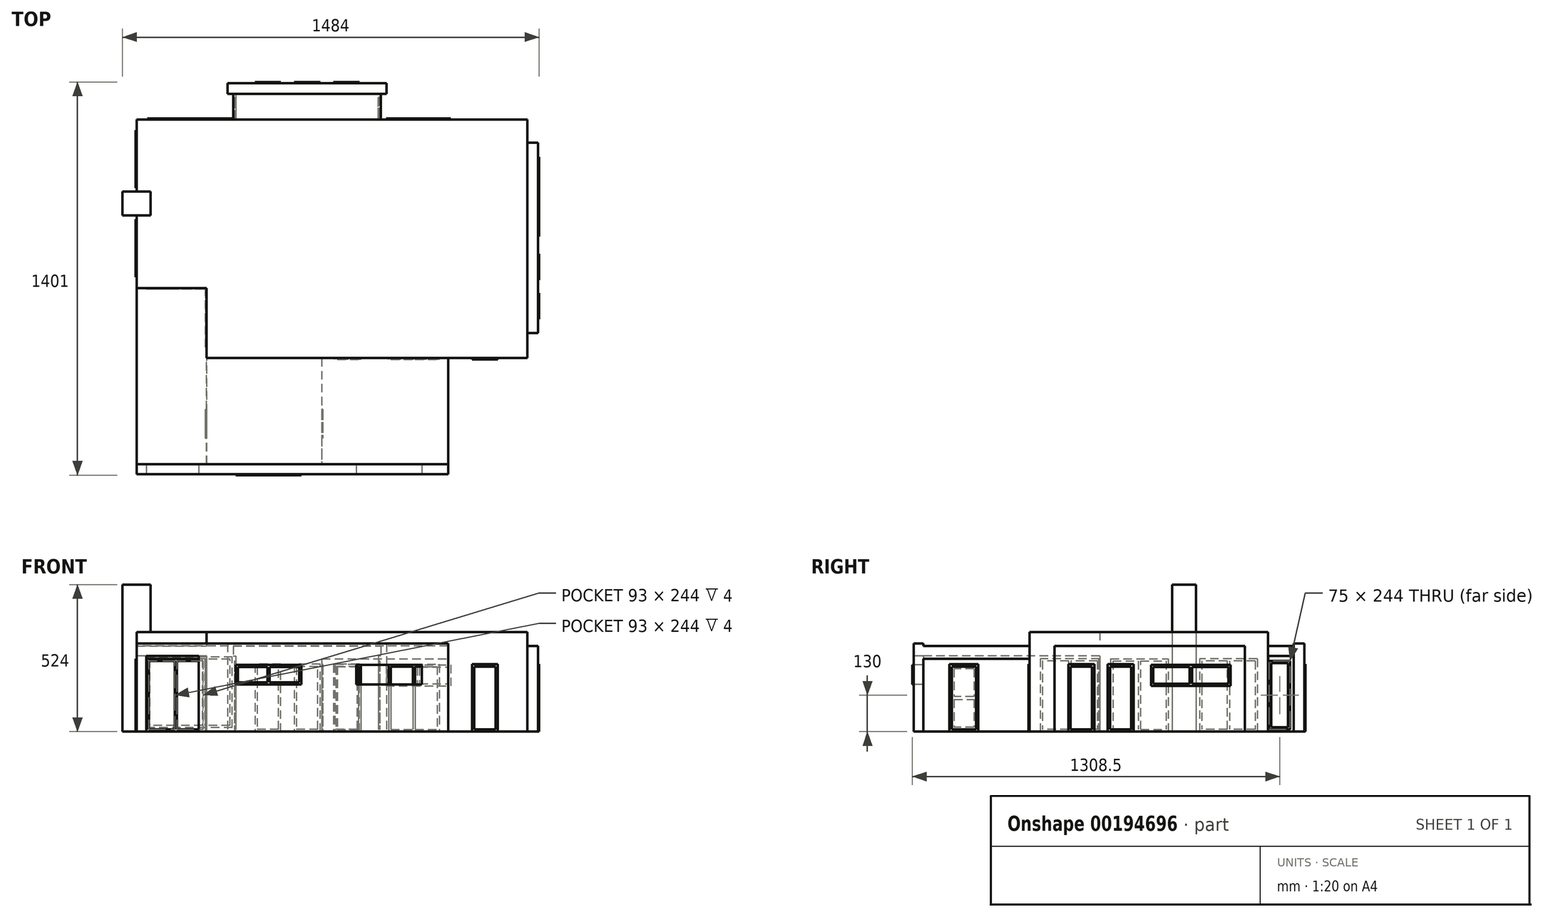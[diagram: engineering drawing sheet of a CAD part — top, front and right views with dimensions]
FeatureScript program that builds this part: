
annotation { "Feature Type Name" : "Feature", "Feature Type Description" : "" }
export const myFeature = defineFeature(function(context is Context, id is Id, definition is map)
    precondition{}
    {
        {
            var Q0;
            Q0=qCreatedBy(makeId("Top.planeOp"),FACE);
            var sketch = newSketch(context, id + "F0", { "sketchPlane" : qUnion([Q0])});
            skLineSegment(sketch, "E0", {"start": v(-692.82, 559.06) * mm, "end": v(699.18, 559.06) * mm});
            skLineSegment(sketch, "E1", {"start": v(699.18, 559.06) * mm, "end": v(699.18, -290.94) * mm});
            skLineSegment(sketch, "E2", {"start": v(699.18, -290.94) * mm, "end": v(-692.82, -290.94) * mm});
            skLineSegment(sketch, "E3", {"start": v(-692.82, -290.94) * mm, "end": v(-692.82, 559.06) * mm});
            skLineSegment(sketch, "E4", {"start": v(-692.82, -40.94) * mm, "end": v(-442.82, -40.94) * mm});
            skLineSegment(sketch, "E5", {"start": v(-442.82, -40.94) * mm, "end": v(-442.82, -290.94) * mm});
            skLineSegment(sketch, "E6", {"start": v(417.18, -290.94) * mm, "end": v(417.18, -668.94) * mm});
            skLineSegment(sketch, "E7", {"start": v(417.18, -668.94) * mm, "end": v(-692.82, -668.94) * mm});
            skLineSegment(sketch, "E8", {"start": v(-692.82, -668.94) * mm, "end": v(-692.82, -290.94) * mm});
            skLineSegment(sketch, "E9", {"start": v(-692.82, 302.06) * mm, "end": v(-642.82, 302.06) * mm});
            skLineSegment(sketch, "E10", {"start": v(-642.82, 302.06) * mm, "end": v(-642.82, 217.06) * mm});
            skLineSegment(sketch, "E11", {"start": v(-642.82, 217.06) * mm, "end": v(-692.82, 217.06) * mm});
            skLineSegment(sketch, "E12.MirrorCS", {"start": v(-692.82, 302.06) * mm, "end": v(-742.82, 302.06) * mm});
            skLineSegment(sketch, "E13.MirrorCS", {"start": v(-742.82, 302.06) * mm, "end": v(-742.82, 217.06) * mm});
            skLineSegment(sketch, "E14.MirrorCS", {"start": v(-742.82, 217.06) * mm, "end": v(-692.82, 217.06) * mm});
            skLineSegment(sketch, "E15", {"start": v(-692.82, -668.94) * mm, "end": v(-692.82, -703.94) * mm});
            skLineSegment(sketch, "E16", {"start": v(-692.82, -703.94) * mm, "end": v(417.18, -703.94) * mm});
            skLineSegment(sketch, "E17", {"start": v(417.18, -703.94) * mm, "end": v(417.18, -668.94) * mm});
            skLineSegment(sketch, "E18", {"start": v(-339.82, 559.06) * mm, "end": v(-339.82, 651.06) * mm});
            skLineSegment(sketch, "E19", {"start": v(-339.82, 651.06) * mm, "end": v(169.18, 651.06) * mm});
            skLineSegment(sketch, "E20", {"start": v(169.18, 651.06) * mm, "end": v(169.18, 559.06) * mm});
            skLineSegment(sketch, "E21", {"start": v(169.18, 651.06) * mm, "end": v(198.18, 651.06) * mm});
            skLineSegment(sketch, "E22", {"start": v(198.18, 651.06) * mm, "end": v(198.18, 689.06) * mm});
            skLineSegment(sketch, "E23", {"start": v(198.18, 689.06) * mm, "end": v(-368.82, 689.06) * mm});
            skLineSegment(sketch, "E24", {"start": v(-368.82, 689.06) * mm, "end": v(-368.82, 651.06) * mm});
            skLineSegment(sketch, "E25", {"start": v(-368.82, 651.06) * mm, "end": v(-339.82, 651.06) * mm});
            skLineSegment(sketch, "E26", {"start": v(699.18, 476.06) * mm, "end": v(737.18, 476.06) * mm});
            skLineSegment(sketch, "E27", {"start": v(737.18, 476.06) * mm, "end": v(737.18, -201.94) * mm});
            skLineSegment(sketch, "E28", {"start": v(737.18, -201.94) * mm, "end": v(699.18, -201.94) * mm});
            skSolve(sketch);
        }
        {
            var Q0;
            {var subQ14=sQuery(id+"F0.wireOp",EDGE,"E4");Q0=makeQuery(id+"F0.imprint","IMPRINT",FACE,{"disambiguationData":[TD([[makeQuery(id+"F0.imprint","IMPRINT",EDGE,{"derivedFrom":subQ14}),1.0]])]});}
            extrude(context, id + "F1", {"entities" : qUnion([Q0]), "depth" : 355 * mm});
        }
        {
            var Q0;
            {var subQ0=sQuery(id+"F0.wireOp",EDGE,"E12.MirrorCS");Q0=makeQuery(id+"F0.imprint","IMPRINT",FACE,{"disambiguationData":[TD([[makeQuery(id+"F0.imprint","IMPRINT",EDGE,{"derivedFrom":subQ0}),1.0]])]});}
            var Q1;
            {var subQ0=sQuery(id+"F0.wireOp",EDGE,"E9");Q1=makeQuery(id+"F0.imprint","IMPRINT",FACE,{"disambiguationData":[TD([[makeQuery(id+"F0.imprint","IMPRINT",EDGE,{"derivedFrom":subQ0}),-1.0]])]});}
            extrude(context, id + "F2", {"entities" : qUnion([Q0, Q1]), "operationType" : NewBodyOperationType.ADD, "depth" : 524 * mm});
        }
        {
            var Q0;
            {var subQ0=sQuery(id+"F0.wireOp",EDGE,"E18");Q0=makeQuery(id+"F0.imprint","IMPRINT",FACE,{"disambiguationData":[TD([[makeQuery(id+"F0.imprint","IMPRINT",EDGE,{"derivedFrom":subQ0}),-1.0]])]});}
            var Q1;
            {var subQ0=sQuery(id+"F0.wireOp",EDGE,"E6");Q1=makeQuery(id+"F0.imprint","IMPRINT",FACE,{"disambiguationData":[TD([[makeQuery(id+"F0.imprint","IMPRINT",EDGE,{"derivedFrom":subQ0}),-1.0]])]});}
            var Q2;
            {var subQ4=sQuery(id+"F0.wireOp",EDGE,"E4");Q2=makeQuery(id+"F0.imprint","IMPRINT",FACE,{"disambiguationData":[TD([[makeQuery(id+"F0.imprint","IMPRINT",EDGE,{"derivedFrom":subQ4}),-1.0]])]});}
            var Q3;
            {var subQ0=sQuery(id+"F0.wireOp",EDGE,"E26");Q3=makeQuery(id+"F0.imprint","IMPRINT",FACE,{"disambiguationData":[TD([[makeQuery(id+"F0.imprint","IMPRINT",EDGE,{"derivedFrom":subQ0}),-1.0]])]});}
            extrude(context, id + "F3", {"entities" : qUnion([Q0, Q1, Q2, Q3]), "operationType" : NewBodyOperationType.ADD, "depth" : 305 * mm});
        }
        {
            var Q0;
            Q0=makeQuery(id+"F0.imprint","IMPRINT",FACE,{"disambiguationData":[TD([[makeQuery(id+"F0.imprint","IMPRINT",EDGE,{"derivedFrom":sQuery(id+"F0.wireOp",EDGE,"E19")}),1.0]])]});
            var Q1;
            Q1=makeQuery(id+"F0.imprint","IMPRINT",FACE,{"disambiguationData":[TD([[makeQuery(id+"F0.imprint","IMPRINT",EDGE,{"derivedFrom":sQuery(id+"F0.wireOp",EDGE,"E7")}),1.0]])]});
            extrude(context, id + "F4", {"entities" : qUnion([Q0, Q1]), "operationType" : NewBodyOperationType.ADD, "depth" : 314 * mm});
        }
        {
            var Q0;
            Q0=makeQuery(id+"F4.boolean.opBoolean","MERGE",FACE,{"derivedFrom":[makeQuery(id+"F3.opExtrude","SWEPT_FACE",FACE,{"disambiguationData":[OSD([sQuery(id+"F0.wireOp",EDGE,"E6")])]}),makeQuery(id+"F4.opExtrude","SWEPT_FACE",FACE,{"disambiguationData":[OSD([sQuery(id+"F0.wireOp",EDGE,"E17")])]})]});
            var sketch = newSketch(context, id + "F5", { "sketchPlane" : qUnion([Q0])});
            skLineSegment(sketch, "E29", {"start": v(-290.94, 260) * mm, "end": v(-668.94, 260) * mm});
            skLineSegment(sketch, "E30", {"start": v(-668.94, 260) * mm, "end": v(-668.94, 0) * mm});
            skSolve(sketch);
        }
        {
            var Q0;
            {var subQ0=sQuery(id+"F5.wireOp",EDGE,"E29");Q0=makeQuery(id+"F5.imprint","IMPRINT",FACE,{"disambiguationData":[TD([[makeQuery(id+"F5.imprint","IMPRINT",EDGE,{"derivedFrom":subQ0}),1.0]])]});}
            extrude(context, id + "F6", {"entities" : qUnion([Q0]), "operationType" : NewBodyOperationType.REMOVE, "oppositeDirection" : true, "depth" : 450 * mm});
        }
        {
            var Q0;
            {var subQ0=sQuery(id+"F0.wireOp",EDGE,"E3");Q0=makeQuery(id+"F4.boolean.opBoolean","MERGE",FACE,{"derivedFrom":[makeQuery(id+"F3.boolean.opBoolean","MERGE",FACE,{"derivedFrom":[makeQuery(id+"F1.opExtrude","SWEPT_FACE",FACE,{"disambiguationData":[OSD([subQ0]),TDD([makeQuery(id+"F0.imprint","IMPRINT",EDGE,{"disambiguationData":[TD([[makeQuery(id+"F0.imprint","INTERSECT",VERTEX,{"derivedFrom":[subQ0,sQuery(id+"F0.wireOp",EDGE,"E4")]}),-1.0]])],"derivedFrom":subQ0})])]}),makeQuery(id+"F3.opExtrude","SWEPT_FACE",FACE,{"disambiguationData":[OSD([subQ0,sQuery(id+"F0.wireOp",EDGE,"E8")])]})]}),makeQuery(id+"F4.opExtrude","SWEPT_FACE",FACE,{"disambiguationData":[OSD([sQuery(id+"F0.wireOp",EDGE,"E15")])]})]});}
            var sketch = newSketch(context, id + "F7", { "sketchPlane" : qUnion([Q0])});
            skLineSegment(sketch, "E31", {"start": v(40.94, 305) * mm, "end": v(40.94, 0) * mm});
            skLineSegment(sketch, "E32", {"start": v(40.94, 270) * mm, "end": v(668.94, 270) * mm});
            skLineSegment(sketch, "E33", {"start": v(668.94, 270) * mm, "end": v(668.94, 0) * mm});
            skSolve(sketch);
        }
        {
            var Q0;
            {var subQ4=sQuery(id+"F7.wireOp",EDGE,"E32");Q0=makeQuery(id+"F7.imprint","IMPRINT",FACE,{"disambiguationData":[TD([[makeQuery(id+"F7.imprint","IMPRINT",EDGE,{"derivedFrom":subQ4}),-1.0]])]});}
            extrude(context, id + "F8", {"entities" : qUnion([Q0]), "operationType" : NewBodyOperationType.REMOVE, "oppositeDirection" : true, "depth" : 250 * mm});
        }
        {
            var Q0;
            Q0=makeQuery(id+"F4.opExtrude","SWEPT_FACE",FACE,{"disambiguationData":[OSD([sQuery(id+"F0.wireOp",EDGE,"E16")])]});
            var sketch = newSketch(context, id + "F9", { "sketchPlane" : qUnion([Q0])});
            skLineSegment(sketch, "E34", {"start": v(-657.82, 0) * mm, "end": v(-657.82, 270) * mm});
            skLineSegment(sketch, "E35", {"start": v(-657.82, 270) * mm, "end": v(-470.82, 270) * mm});
            skLineSegment(sketch, "E36", {"start": v(-470.82, 270) * mm, "end": v(-470.82, 0) * mm});
            skLineSegment(sketch, "E37", {"start": v(90.18, 238) * mm, "end": v(324.18, 238) * mm});
            skLineSegment(sketch, "E38", {"start": v(324.18, 238) * mm, "end": v(324.18, 168) * mm});
            skLineSegment(sketch, "E39", {"start": v(90.18, 238) * mm, "end": v(90.18, 168) * mm});
            skLineSegment(sketch, "E40", {"start": v(90.18, 168) * mm, "end": v(324.18, 168) * mm});
            skSolve(sketch);
        }
        {
            var Q0;
            {var subQ0=sQuery(id+"F9.wireOp",EDGE,"E34");Q0=makeQuery(id+"F9.imprint","IMPRINT",FACE,{"disambiguationData":[TD([[makeQuery(id+"F9.imprint","IMPRINT",EDGE,{"derivedFrom":subQ0}),-1.0]])]});}
            var Q1;
            Q1=makeQuery(id+"F9.imprint","IMPRINT",FACE,{"disambiguationData":[TD([[makeQuery(id+"F9.imprint","IMPRINT",EDGE,{"derivedFrom":sQuery(id+"F9.wireOp",EDGE,"E37")}),-1.0]])]});
            var Q2;
            Q2=makeQuery(id+"F8.boolean.opBoolean","COPY",FACE,{"derivedFrom":makeQuery(id+"F8.opExtrude","SWEPT_FACE",FACE,{"disambiguationData":[OSD([sQuery(id+"F7.wireOp",EDGE,"E33")])]})});
            extrude(context, id + "F10", {"entities" : qUnion([Q0, Q1]), "operationType" : NewBodyOperationType.REMOVE, "endBound" : BoundingType.UP_TO_SURFACE, "oppositeDirection" : true, "endBoundEntityFace" : qUnion([Q2]), "depth" : 25 * mm});
        }
        {
            var Q0;
            Q0=makeQuery(id+"F4.opExtrude","SWEPT_FACE",FACE,{"disambiguationData":[OSD([sQuery(id+"F0.wireOp",EDGE,"E23")])]});
            var sketch = newSketch(context, id + "F11", { "sketchPlane" : qUnion([Q0])});
            skLineSegment(sketch, "E41", {"start": v(-101.18, 0) * mm, "end": v(-101.18, 240) * mm});
            skLineSegment(sketch, "E42", {"start": v(-101.18, 240) * mm, "end": v(-9.18, 240) * mm});
            skLineSegment(sketch, "E43", {"start": v(-9.18, 240) * mm, "end": v(-9.18, 0) * mm});
            skLineSegment(sketch, "E44", {"start": v(38.82, 0) * mm, "end": v(38.82, 240) * mm});
            skLineSegment(sketch, "E45", {"start": v(38.82, 240) * mm, "end": v(130.82, 240) * mm});
            skLineSegment(sketch, "E46", {"start": v(130.82, 240) * mm, "end": v(130.82, 0) * mm});
            skLineSegment(sketch, "E47", {"start": v(178.82, 0) * mm, "end": v(178.82, 240) * mm});
            skLineSegment(sketch, "E48", {"start": v(178.82, 240) * mm, "end": v(270.82, 240) * mm});
            skLineSegment(sketch, "E49", {"start": v(270.82, 240) * mm, "end": v(270.82, 0) * mm});
            skLineSegment(sketch, "E50", {"start": v(-101.18, 0) * mm, "end": v(-9.18, 0) * mm});
            skLineSegment(sketch, "E51", {"start": v(38.82, 0) * mm, "end": v(130.82, 0) * mm});
            skLineSegment(sketch, "E52", {"start": v(178.82, 0) * mm, "end": v(270.82, 0) * mm});
            skLineSegment(sketch, "E53.0", {"start": v(-93.18, 8) * mm, "end": v(-93.18, 232) * mm});
            skLineSegment(sketch, "E53.1", {"start": v(-93.18, 8) * mm, "end": v(-17.18, 8) * mm});
            skLineSegment(sketch, "E53.2", {"start": v(-17.18, 232) * mm, "end": v(-17.18, 8) * mm});
            skLineSegment(sketch, "E53.3", {"start": v(-93.18, 232) * mm, "end": v(-17.18, 232) * mm});
            skLineSegment(sketch, "E54.0", {"start": v(46.82, 8) * mm, "end": v(46.82, 232) * mm});
            skLineSegment(sketch, "E54.1", {"start": v(46.82, 8) * mm, "end": v(122.82, 8) * mm});
            skLineSegment(sketch, "E54.2", {"start": v(122.82, 232) * mm, "end": v(122.82, 8) * mm});
            skLineSegment(sketch, "E54.3", {"start": v(46.82, 232) * mm, "end": v(122.82, 232) * mm});
            skLineSegment(sketch, "E55.0", {"start": v(186.82, 8) * mm, "end": v(186.82, 232) * mm});
            skLineSegment(sketch, "E55.1", {"start": v(186.82, 8) * mm, "end": v(262.82, 8) * mm});
            skLineSegment(sketch, "E55.2", {"start": v(262.82, 232) * mm, "end": v(262.82, 8) * mm});
            skLineSegment(sketch, "E55.3", {"start": v(186.82, 232) * mm, "end": v(262.82, 232) * mm});
            skSolve(sketch);
        }
        {
            var Q0;
            Q0=makeQuery(id+"F3.opExtrude","SWEPT_FACE",FACE,{"disambiguationData":[OSD([sQuery(id+"F0.wireOp",EDGE,"E20")])]});
            var sketch = newSketch(context, id + "F12", { "sketchPlane" : qUnion([Q0])});
            skLineSegment(sketch, "E56.bottom", {"start": v(563.06, 252) * mm, "end": v(638.06, 252) * mm});
            skLineSegment(sketch, "E56.left", {"start": v(563.06, 252) * mm, "end": v(563.06, 8) * mm});
            skLineSegment(sketch, "E56.right", {"start": v(638.06, 252) * mm, "end": v(638.06, 8) * mm});
            skLineSegment(sketch, "E57", {"start": v(563.06, 8) * mm, "end": v(638.06, 8) * mm});
            skLineSegment(sketch, "E58.0", {"start": v(571.06, 244) * mm, "end": v(630.06, 244) * mm});
            skLineSegment(sketch, "E58.1", {"start": v(571.06, 244) * mm, "end": v(571.06, 16) * mm});
            skLineSegment(sketch, "E58.2", {"start": v(571.06, 16) * mm, "end": v(630.06, 16) * mm});
            skLineSegment(sketch, "E58.3", {"start": v(630.06, 244) * mm, "end": v(630.06, 16) * mm});
            skLineSegment(sketch, "E59", {"start": v(559.06, 270) * mm, "end": v(651.06, 270) * mm});
            skSolve(sketch);
        }
        {
            var Q0;
            {var subQ0=sQuery(id+"F12.wireOp",EDGE,"E59");Q0=makeQuery(id+"F12.imprint","IMPRINT",FACE,{"disambiguationData":[TD([[makeQuery(id+"F12.imprint","IMPRINT",EDGE,{"derivedFrom":subQ0}),1.0]])]});}
            extrude(context, id + "F13", {"entities" : qUnion([Q0]), "operationType" : NewBodyOperationType.ADD, "depth" : 8 * mm});
        }
        {
            var Q0;
            Q0=makeQuery(id+"F3.opExtrude","SWEPT_FACE",FACE,{"disambiguationData":[OSD([sQuery(id+"F0.wireOp",EDGE,"E18")])]});
            var sketch = newSketch(context, id + "F14", { "sketchPlane" : qUnion([Q0])});
            skLineSegment(sketch, "E60.bottom", {"start": v(-638.06, 252) * mm, "end": v(-563.06, 252) * mm});
            skLineSegment(sketch, "E60.left", {"start": v(-638.06, 252) * mm, "end": v(-638.06, 8) * mm});
            skLineSegment(sketch, "E60.right", {"start": v(-563.06, 252) * mm, "end": v(-563.06, 8) * mm});
            skLineSegment(sketch, "E61", {"start": v(-638.06, 8) * mm, "end": v(-563.06, 8) * mm});
            skLineSegment(sketch, "E62.0", {"start": v(-630.06, 244) * mm, "end": v(-571.06, 244) * mm});
            skLineSegment(sketch, "E62.1", {"start": v(-630.06, 244) * mm, "end": v(-630.06, 16) * mm});
            skLineSegment(sketch, "E62.2", {"start": v(-630.06, 16) * mm, "end": v(-571.06, 16) * mm});
            skLineSegment(sketch, "E62.3", {"start": v(-571.06, 244) * mm, "end": v(-571.06, 16) * mm});
            skLineSegment(sketch, "E63", {"start": v(-651.06, 270) * mm, "end": v(-559.06, 270) * mm});
            skSolve(sketch);
        }
        {
            var Q0;
            {var subQ0=sQuery(id+"F14.wireOp",EDGE,"E63");Q0=makeQuery(id+"F14.imprint","IMPRINT",FACE,{"disambiguationData":[TD([[makeQuery(id+"F14.imprint","IMPRINT",EDGE,{"derivedFrom":subQ0}),1.0]])]});}
            extrude(context, id + "F15", {"entities" : qUnion([Q0]), "operationType" : NewBodyOperationType.ADD, "depth" : 8 * mm});
        }
        {
            var Q0;
            Q0=makeQuery(id+"F1.opExtrude","SWEPT_FACE",FACE,{"disambiguationData":[OSD([sQuery(id+"F0.wireOp",EDGE,"E0")])]});
            var sketch = newSketch(context, id + "F16", { "sketchPlane" : qUnion([Q0])});
            skLineSegment(sketch, "E64", {"start": v(351.82, 14) * mm, "end": v(351.82, 266) * mm});
            skLineSegment(sketch, "E65", {"start": v(351.82, 266) * mm, "end": v(654.82, 266) * mm});
            skLineSegment(sketch, "E66", {"start": v(654.82, 266) * mm, "end": v(654.82, 14) * mm});
            skLineSegment(sketch, "E67", {"start": v(351.82, 14) * mm, "end": v(654.82, 14) * mm});
            skPoint(sketch, "E68.orphan", {"position": v(654.82, 0) * mm});
            skLineSegment(sketch, "E69.0", {"start": v(359.82, 22) * mm, "end": v(359.82, 258) * mm});
            skLineSegment(sketch, "E69.1", {"start": v(359.82, 22) * mm, "end": v(450.12, 22) * mm});
            skLineSegment(sketch, "E69.2", {"start": v(646.82, 258) * mm, "end": v(646.82, 22) * mm});
            skLineSegment(sketch, "E69.3", {"start": v(359.82, 258) * mm, "end": v(450.12, 258) * mm});
            skLineSegment(sketch, "E70", {"start": v(458.12, 258) * mm, "end": v(458.12, 22) * mm});
            skLineSegment(sketch, "E71", {"start": v(548.52, 258) * mm, "end": v(548.52, 22) * mm});
            skLineSegment(sketch, "E72", {"start": v(556.52, 258) * mm, "end": v(556.52, 22) * mm});
            skLineSegment(sketch, "E73", {"start": v(450.12, 258) * mm, "end": v(450.12, 22) * mm});
            skLineSegment(sketch, "E74.trimOffspring", {"start": v(458.12, 258) * mm, "end": v(548.52, 258) * mm});
            skLineSegment(sketch, "E75.trimOffspring", {"start": v(556.52, 258) * mm, "end": v(646.82, 258) * mm});
            skLineSegment(sketch, "E76.trimOffspring", {"start": v(556.52, 22) * mm, "end": v(646.82, 22) * mm});
            skLineSegment(sketch, "E77.trimOffspring", {"start": v(458.12, 22) * mm, "end": v(548.52, 22) * mm});
            skLineSegment(sketch, "E78.bottom", {"start": v(-196.18, 238) * mm, "end": v(-426.18, 238) * mm});
            skLineSegment(sketch, "E78.top", {"start": v(-196.18, 163) * mm, "end": v(-426.18, 163) * mm});
            skLineSegment(sketch, "E78.left", {"start": v(-196.18, 238) * mm, "end": v(-196.18, 163) * mm});
            skLineSegment(sketch, "E78.right", {"start": v(-426.18, 238) * mm, "end": v(-426.18, 163) * mm});
            skLineSegment(sketch, "E79.0", {"start": v(-418.18, 230) * mm, "end": v(-418.18, 171) * mm});
            skLineSegment(sketch, "E79.1", {"start": v(-204.18, 230) * mm, "end": v(-307.18, 230) * mm});
            skLineSegment(sketch, "E79.2", {"start": v(-204.18, 230) * mm, "end": v(-204.18, 171) * mm});
            skLineSegment(sketch, "E79.3", {"start": v(-204.18, 171) * mm, "end": v(-307.18, 171) * mm});
            skLineSegment(sketch, "E80", {"start": v(-315.18, 230) * mm, "end": v(-315.18, 171) * mm});
            skLineSegment(sketch, "E81", {"start": v(-307.18, 230) * mm, "end": v(-307.18, 171) * mm});
            skLineSegment(sketch, "E82.trimOffspring", {"start": v(-315.18, 230) * mm, "end": v(-418.18, 230) * mm});
            skLineSegment(sketch, "E83.trimOffspring", {"start": v(-315.18, 171) * mm, "end": v(-418.18, 171) * mm});
            skSolve(sketch);
        }
        {
            var Q0;
            Q0=makeQuery(id+"F3.opExtrude","SWEPT_FACE",FACE,{"disambiguationData":[OSD([sQuery(id+"F0.wireOp",EDGE,"E27")])]});
            var sketch = newSketch(context, id + "F17", { "sketchPlane" : qUnion([Q0])});
            skLineSegment(sketch, "E84.bottom", {"start": v(-151.94, 240) * mm, "end": v(-59.94, 240) * mm});
            skLineSegment(sketch, "E84.top", {"start": v(-151.94, 0) * mm, "end": v(-59.94, 0) * mm});
            skLineSegment(sketch, "E84.left", {"start": v(-151.94, 240) * mm, "end": v(-151.94, 0) * mm});
            skLineSegment(sketch, "E84.right", {"start": v(-59.94, 240) * mm, "end": v(-59.94, 0) * mm});
            skLineSegment(sketch, "E85.bottom", {"start": v(-11.94, 240) * mm, "end": v(80.06, 240) * mm});
            skLineSegment(sketch, "E85.top", {"start": v(-11.94, 0) * mm, "end": v(80.06, 0) * mm});
            skLineSegment(sketch, "E85.left", {"start": v(-11.94, 240) * mm, "end": v(-11.94, 0) * mm});
            skLineSegment(sketch, "E85.right", {"start": v(80.06, 240) * mm, "end": v(80.06, 0) * mm});
            skLineSegment(sketch, "E86.bottom", {"start": v(142.06, 238) * mm, "end": v(426.06, 238) * mm});
            skLineSegment(sketch, "E86.top", {"start": v(142.06, 163) * mm, "end": v(426.06, 163) * mm});
            skLineSegment(sketch, "E86.left", {"start": v(142.06, 238) * mm, "end": v(142.06, 163) * mm});
            skLineSegment(sketch, "E86.right", {"start": v(426.06, 238) * mm, "end": v(426.06, 163) * mm});
            skLineSegment(sketch, "E87.0", {"start": v(150.06, 230) * mm, "end": v(150.06, 171) * mm});
            skLineSegment(sketch, "E87.1", {"start": v(150.06, 230) * mm, "end": v(280.06, 230) * mm});
            skLineSegment(sketch, "E87.2", {"start": v(418.06, 230) * mm, "end": v(418.06, 171) * mm});
            skLineSegment(sketch, "E87.3", {"start": v(150.06, 171) * mm, "end": v(280.06, 171) * mm});
            skLineSegment(sketch, "E88", {"start": v(288.06, 230) * mm, "end": v(288.06, 171) * mm});
            skLineSegment(sketch, "E89", {"start": v(280.06, 230) * mm, "end": v(280.06, 171) * mm});
            skLineSegment(sketch, "E90.trimOffspring", {"start": v(288.06, 230) * mm, "end": v(418.06, 230) * mm});
            skLineSegment(sketch, "E91.trimOffspring", {"start": v(288.06, 171) * mm, "end": v(418.06, 171) * mm});
            skLineSegment(sketch, "E92.0", {"start": v(-143.94, 8) * mm, "end": v(-67.94, 8) * mm});
            skLineSegment(sketch, "E92.1", {"start": v(-143.94, 232) * mm, "end": v(-143.94, 8) * mm});
            skLineSegment(sketch, "E92.2", {"start": v(-143.94, 232) * mm, "end": v(-67.94, 232) * mm});
            skLineSegment(sketch, "E92.3", {"start": v(-67.94, 232) * mm, "end": v(-67.94, 8) * mm});
            skLineSegment(sketch, "E93.0", {"start": v(-3.94, 232) * mm, "end": v(72.06, 232) * mm});
            skLineSegment(sketch, "E93.1", {"start": v(-3.94, 232) * mm, "end": v(-3.94, 8) * mm});
            skLineSegment(sketch, "E93.2", {"start": v(-3.94, 8) * mm, "end": v(72.06, 8) * mm});
            skLineSegment(sketch, "E93.3", {"start": v(72.06, 232) * mm, "end": v(72.06, 8) * mm});
            skSolve(sketch);
        }
        {
            var Q0;
            {var subQ0=sQuery(id+"F0.wireOp",EDGE,"E3");Q0=makeQuery(id+"F1.opExtrude","SWEPT_FACE",FACE,{"disambiguationData":[OSD([subQ0]),TDD([makeQuery(id+"F0.imprint","IMPRINT",EDGE,{"disambiguationData":[TD([[makeQuery(id+"F0.imprint","INTERSECT",VERTEX,{"derivedFrom":[sQuery(id+"F0.wireOp",EDGE,"E0"),subQ0]}),1.0]])],"derivedFrom":subQ0})])]});}
            var sketch = newSketch(context, id + "F18", { "sketchPlane" : qUnion([Q0])});
            skPoint(sketch, "E94.0", {"position": v(-259.56, 524) * mm});
            skLineSegment(sketch, "E95", {"start": v(-259.56, 524) * mm, "end": v(-259.56, 0) * mm, "construction": true});
            skLineSegment(sketch, "E96.bottom", {"start": v(-521.06, 260) * mm, "end": v(-315.06, 260) * mm});
            skLineSegment(sketch, "E96.top", {"start": v(-521.06, 0) * mm, "end": v(-315.06, 0) * mm});
            skLineSegment(sketch, "E96.left", {"start": v(-521.06, 260) * mm, "end": v(-521.06, 0) * mm});
            skLineSegment(sketch, "E96.right", {"start": v(-315.06, 260) * mm, "end": v(-315.06, 0) * mm});
            skLineSegment(sketch, "E97.0", {"start": v(-513.06, 252) * mm, "end": v(-422.06, 252) * mm});
            skLineSegment(sketch, "E97.1", {"start": v(-513.06, 252) * mm, "end": v(-513.06, 8) * mm});
            skLineSegment(sketch, "E97.2", {"start": v(-513.06, 8) * mm, "end": v(-422.06, 8) * mm});
            skLineSegment(sketch, "E97.3", {"start": v(-323.06, 252) * mm, "end": v(-323.06, 8) * mm});
            skLineSegment(sketch, "E98", {"start": v(-422.06, 252) * mm, "end": v(-422.06, 8) * mm});
            skLineSegment(sketch, "E99", {"start": v(-414.06, 8) * mm, "end": v(-414.06, 252) * mm});
            skLineSegment(sketch, "E100.trimOffspring", {"start": v(-414.06, 252) * mm, "end": v(-323.06, 252) * mm});
            skLineSegment(sketch, "E101.trimOffspring", {"start": v(-414.06, 8) * mm, "end": v(-323.06, 8) * mm});
            skLineSegment(sketch, "E102.MirrorCS", {"start": v(-105.06, 8) * mm, "end": v(-196.06, 8) * mm});
            skLineSegment(sketch, "E103.MirrorCS", {"start": v(1.94, 260) * mm, "end": v(-204.06, 260) * mm});
            skLineSegment(sketch, "E104.MirrorCS", {"start": v(1.94, 0) * mm, "end": v(-204.06, 0) * mm});
            skLineSegment(sketch, "E105.MirrorCS", {"start": v(1.94, 260) * mm, "end": v(1.94, 0) * mm});
            skLineSegment(sketch, "E106.MirrorCS", {"start": v(-204.06, 260) * mm, "end": v(-204.06, 0) * mm});
            skLineSegment(sketch, "E107.MirrorCS", {"start": v(-6.06, 252) * mm, "end": v(-97.06, 252) * mm});
            skLineSegment(sketch, "E108.MirrorCS", {"start": v(-6.06, 252) * mm, "end": v(-6.06, 8) * mm});
            skLineSegment(sketch, "E109.MirrorCS", {"start": v(-97.06, 252) * mm, "end": v(-97.06, 8) * mm});
            skLineSegment(sketch, "E110.MirrorCS", {"start": v(-196.06, 252) * mm, "end": v(-196.06, 8) * mm});
            skLineSegment(sketch, "E111.MirrorCS", {"start": v(-6.06, 8) * mm, "end": v(-97.06, 8) * mm});
            skLineSegment(sketch, "E112.MirrorCS", {"start": v(-105.06, 252) * mm, "end": v(-196.06, 252) * mm});
            skLineSegment(sketch, "E113.MirrorCS", {"start": v(-105.06, 8) * mm, "end": v(-105.06, 252) * mm});
            skSolve(sketch);
        }
        {
            var Q0;
            Q0=makeQuery(id+"F8.boolean.opBoolean","COPY",FACE,{"derivedFrom":makeQuery(id+"F8.opExtrude","SWEPT_FACE",FACE,{"disambiguationData":[OSD([sQuery(id+"F7.wireOp",EDGE,"E31")])]})});
            var sketch = newSketch(context, id + "F19", { "sketchPlane" : qUnion([Q0])});
            skLineSegment(sketch, "E114.bottom", {"start": v(-447.82, 260) * mm, "end": v(-657.82, 260) * mm});
            skLineSegment(sketch, "E114.top", {"start": v(-447.82, 0) * mm, "end": v(-657.82, 0) * mm});
            skLineSegment(sketch, "E114.left", {"start": v(-447.82, 260) * mm, "end": v(-447.82, 0) * mm});
            skLineSegment(sketch, "E114.right", {"start": v(-657.82, 260) * mm, "end": v(-657.82, 0) * mm});
            skLineSegment(sketch, "E115.0", {"start": v(-649.82, 252) * mm, "end": v(-649.82, 8) * mm});
            skLineSegment(sketch, "E115.1", {"start": v(-455.82, 252) * mm, "end": v(-548.82, 252) * mm});
            skLineSegment(sketch, "E115.2", {"start": v(-455.82, 252) * mm, "end": v(-455.82, 8) * mm});
            skLineSegment(sketch, "E115.3", {"start": v(-455.82, 8) * mm, "end": v(-548.82, 8) * mm});
            skLineSegment(sketch, "E116", {"start": v(-556.82, 252) * mm, "end": v(-556.82, 8) * mm});
            skLineSegment(sketch, "E117", {"start": v(-548.82, 8) * mm, "end": v(-548.82, 252) * mm});
            skLineSegment(sketch, "E118.trimOffspring", {"start": v(-556.82, 252) * mm, "end": v(-649.82, 252) * mm});
            skLineSegment(sketch, "E119.trimOffspring", {"start": v(-556.82, 8) * mm, "end": v(-649.82, 8) * mm});
            skSolve(sketch);
        }
        {
            var Q0;
            Q0=makeQuery(id+"F8.boolean.opBoolean","COPY",FACE,{"derivedFrom":makeQuery(id+"F8.opExtrude","CAP_FACE",FACE,{"disambiguationData":[OSD([sQuery(id+"F0.wireOp",EDGE,"E3"),sQuery(id+"F0.wireOp",EDGE,"E8"),sQuery(id+"F0.wireOp",EDGE,"E15"),sQuery(id+"F7.wireOp",EDGE,"E31"),sQuery(id+"F7.wireOp",EDGE,"E32"),sQuery(id+"F7.wireOp",EDGE,"E33")])],"isStart":false})});
            var sketch = newSketch(context, id + "F20", { "sketchPlane" : qUnion([Q0])});
            skLineSegment(sketch, "E120.bottom", {"start": v(40.94, 260) * mm, "end": v(252.94, 260) * mm});
            skLineSegment(sketch, "E120.top", {"start": v(40.94, 0) * mm, "end": v(252.94, 0) * mm});
            skLineSegment(sketch, "E120.left", {"start": v(40.94, 260) * mm, "end": v(40.94, 0) * mm});
            skLineSegment(sketch, "E120.right", {"start": v(252.94, 260) * mm, "end": v(252.94, 0) * mm});
            skLineSegment(sketch, "E121.0", {"start": v(48.94, 252) * mm, "end": v(48.94, 8) * mm});
            skLineSegment(sketch, "E121.1", {"start": v(48.94, 252) * mm, "end": v(142.94, 252) * mm});
            skLineSegment(sketch, "E121.2", {"start": v(244.94, 252) * mm, "end": v(244.94, 8) * mm});
            skLineSegment(sketch, "E121.3", {"start": v(48.94, 8) * mm, "end": v(142.94, 8) * mm});
            skLineSegment(sketch, "E122", {"start": v(142.94, 252) * mm, "end": v(142.94, 8) * mm});
            skLineSegment(sketch, "E123", {"start": v(150.94, 8) * mm, "end": v(150.94, 252) * mm});
            skLineSegment(sketch, "E124.trimOffspring", {"start": v(150.94, 252) * mm, "end": v(244.94, 252) * mm});
            skLineSegment(sketch, "E125.trimOffspring", {"start": v(150.94, 8) * mm, "end": v(244.94, 8) * mm});
            skLineSegment(sketch, "E126.bottom", {"start": v(472.94, 240) * mm, "end": v(575.94, 240) * mm});
            skLineSegment(sketch, "E126.top", {"start": v(472.94, 0) * mm, "end": v(575.94, 0) * mm});
            skLineSegment(sketch, "E126.left", {"start": v(472.94, 240) * mm, "end": v(472.94, 0) * mm});
            skLineSegment(sketch, "E126.right", {"start": v(575.94, 240) * mm, "end": v(575.94, 0) * mm});
            skLineSegment(sketch, "E127", {"start": v(488.94, 125.5) * mm, "end": v(559.94, 125.5) * mm});
            skLineSegment(sketch, "E128", {"start": v(559.94, 114.5) * mm, "end": v(488.94, 114.5) * mm});
            skLineSegment(sketch, "E129.0", {"start": v(480.94, 232) * mm, "end": v(480.94, 8) * mm});
            skLineSegment(sketch, "E129.1", {"start": v(480.94, 232) * mm, "end": v(567.94, 232) * mm});
            skLineSegment(sketch, "E129.2", {"start": v(567.94, 232) * mm, "end": v(567.94, 8) * mm});
            skLineSegment(sketch, "E129.3", {"start": v(480.94, 8) * mm, "end": v(567.94, 8) * mm});
            skLineSegment(sketch, "E130.0", {"start": v(559.94, 224) * mm, "end": v(559.94, 125.5) * mm});
            skLineSegment(sketch, "E130.1", {"start": v(488.94, 224) * mm, "end": v(559.94, 224) * mm});
            skLineSegment(sketch, "E130.2", {"start": v(488.94, 224) * mm, "end": v(488.94, 125.5) * mm});
            skLineSegment(sketch, "E130.3", {"start": v(488.94, 16) * mm, "end": v(559.94, 16) * mm});
            skLineSegment(sketch, "E131.trimOffspring", {"start": v(488.94, 114.5) * mm, "end": v(488.94, 16) * mm});
            skLineSegment(sketch, "E132.trimOffspring", {"start": v(559.94, 114.5) * mm, "end": v(559.94, 16) * mm});
            skSolve(sketch);
        }
        {
            var Q0;
            Q0=makeQuery(id+"F4.opExtrude","SWEPT_FACE",FACE,{"disambiguationData":[OSD([sQuery(id+"F0.wireOp",EDGE,"E16")])]});
            var sketch = newSketch(context, id + "F21", { "sketchPlane" : qUnion([Q0])});
            skLineSegment(sketch, "E133.bottom", {"start": v(-105.82, 168) * mm, "end": v(-339.82, 168) * mm});
            skLineSegment(sketch, "E133.top", {"start": v(-105.82, 238) * mm, "end": v(-339.82, 238) * mm});
            skLineSegment(sketch, "E133.left", {"start": v(-105.82, 168) * mm, "end": v(-105.82, 238) * mm});
            skLineSegment(sketch, "E133.right", {"start": v(-339.82, 168) * mm, "end": v(-339.82, 238) * mm});
            skLineSegment(sketch, "E134.0", {"start": v(-113.82, 230) * mm, "end": v(-218.82, 230) * mm});
            skLineSegment(sketch, "E134.1", {"start": v(-113.82, 176) * mm, "end": v(-113.82, 230) * mm});
            skLineSegment(sketch, "E134.2", {"start": v(-113.82, 176) * mm, "end": v(-218.82, 176) * mm});
            skLineSegment(sketch, "E134.3", {"start": v(-331.82, 176) * mm, "end": v(-331.82, 230) * mm});
            skLineSegment(sketch, "E135", {"start": v(-226.82, 230) * mm, "end": v(-226.82, 176) * mm});
            skLineSegment(sketch, "E136", {"start": v(-218.82, 230) * mm, "end": v(-218.82, 176) * mm});
            skLineSegment(sketch, "E137.trimOffspring", {"start": v(-226.82, 230) * mm, "end": v(-331.82, 230) * mm});
            skLineSegment(sketch, "E138.trimOffspring", {"start": v(-226.82, 176) * mm, "end": v(-331.82, 176) * mm});
            skSolve(sketch);
        }
        {
            var Q0;
            Q0=makeQuery(id+"F6.boolean.opBoolean","COPY",FACE,{"derivedFrom":makeQuery(id+"F6.opExtrude","CAP_FACE",FACE,{"disambiguationData":[OSD([sQuery(id+"F0.wireOp",EDGE,"E2"),sQuery(id+"F0.wireOp",EDGE,"E6"),sQuery(id+"F0.wireOp",EDGE,"E17"),sQuery(id+"F5.wireOp",EDGE,"E29"),sQuery(id+"F5.wireOp",EDGE,"E30")])],"isStart":false})});
            var sketch = newSketch(context, id + "F22", { "sketchPlane" : qUnion([Q0])});
            skLineSegment(sketch, "E139.0", {"start": v(-472.94, 240) * mm, "end": v(-575.94, 240) * mm});
            skLineSegment(sketch, "E140.0", {"start": v(-480.94, 232) * mm, "end": v(-567.94, 232) * mm});
            skLineSegment(sketch, "E140.1", {"start": v(-575.94, 240) * mm, "end": v(-575.94, 0) * mm});
            skLineSegment(sketch, "E140.2", {"start": v(-567.94, 232) * mm, "end": v(-567.94, 8) * mm});
            skLineSegment(sketch, "E140.3", {"start": v(-559.94, 224) * mm, "end": v(-559.94, 125.5) * mm});
            skLineSegment(sketch, "E140.4", {"start": v(-488.94, 125.5) * mm, "end": v(-559.94, 125.5) * mm});
            skLineSegment(sketch, "E140.5", {"start": v(-559.94, 114.5) * mm, "end": v(-488.94, 114.5) * mm});
            skLineSegment(sketch, "E140.6", {"start": v(-559.94, 114.5) * mm, "end": v(-559.94, 16) * mm});
            skLineSegment(sketch, "E140.7", {"start": v(-480.94, 8) * mm, "end": v(-567.94, 8) * mm});
            skLineSegment(sketch, "E140.8", {"start": v(-488.94, 16) * mm, "end": v(-559.94, 16) * mm});
            skLineSegment(sketch, "E140.9", {"start": v(-472.94, 240) * mm, "end": v(-472.94, 0) * mm});
            skLineSegment(sketch, "E140.10", {"start": v(-472.94, 0) * mm, "end": v(-575.94, 0) * mm});
            skLineSegment(sketch, "E140.11", {"start": v(-480.94, 232) * mm, "end": v(-480.94, 8) * mm});
            skLineSegment(sketch, "E140.12", {"start": v(-488.94, 114.5) * mm, "end": v(-488.94, 16) * mm});
            skLineSegment(sketch, "E140.13", {"start": v(-488.94, 224) * mm, "end": v(-488.94, 125.5) * mm});
            skLineSegment(sketch, "E140.14", {"start": v(-488.94, 224) * mm, "end": v(-559.94, 224) * mm});
            skSolve(sketch);
        }
        {
            var Q0;
            {var subQ0=sQuery(id+"F0.wireOp",EDGE,"E2");Q0=makeQuery(id+"F6.boolean.opBoolean","MERGE",FACE,{"derivedFrom":[makeQuery(id+"F1.opExtrude","SWEPT_FACE",FACE,{"disambiguationData":[OSD([subQ0])]}),makeQuery(id+"F6.opExtrude","SWEPT_FACE",FACE,{"disambiguationData":[OSD([subQ0,sQuery(id+"F0.wireOp",EDGE,"E6")])]})]});}
            var sketch = newSketch(context, id + "F23", { "sketchPlane" : qUnion([Q0])});
            skLineSegment(sketch, "E141.bottom", {"start": v(14.18, 240) * mm, "end": v(106.18, 240) * mm});
            skLineSegment(sketch, "E141.top", {"start": v(14.18, 0) * mm, "end": v(106.18, 0) * mm});
            skLineSegment(sketch, "E141.left", {"start": v(14.18, 240) * mm, "end": v(14.18, 0) * mm});
            skLineSegment(sketch, "E141.right", {"start": v(106.18, 240) * mm, "end": v(106.18, 0) * mm});
            skLineSegment(sketch, "E142.0", {"start": v(22.18, 232) * mm, "end": v(22.18, 8) * mm});
            skLineSegment(sketch, "E142.1", {"start": v(22.18, 232) * mm, "end": v(98.18, 232) * mm});
            skLineSegment(sketch, "E142.2", {"start": v(98.18, 232) * mm, "end": v(98.18, 8) * mm});
            skLineSegment(sketch, "E142.3", {"start": v(22.18, 8) * mm, "end": v(98.18, 8) * mm});
            skLineSegment(sketch, "E143.bottom", {"start": v(205.18, 240) * mm, "end": v(386.18, 240) * mm});
            skLineSegment(sketch, "E143.top", {"start": v(205.18, 0) * mm, "end": v(386.18, 0) * mm});
            skLineSegment(sketch, "E143.left", {"start": v(205.18, 240) * mm, "end": v(205.18, 0) * mm});
            skLineSegment(sketch, "E143.right", {"start": v(386.18, 240) * mm, "end": v(386.18, 0) * mm});
            skLineSegment(sketch, "E144.bottom", {"start": v(502.18, 240) * mm, "end": v(594.18, 240) * mm});
            skLineSegment(sketch, "E144.top", {"start": v(502.18, 0) * mm, "end": v(594.18, 0) * mm});
            skLineSegment(sketch, "E144.left", {"start": v(502.18, 240) * mm, "end": v(502.18, 0) * mm});
            skLineSegment(sketch, "E144.right", {"start": v(594.18, 240) * mm, "end": v(594.18, 0) * mm});
            skLineSegment(sketch, "E145.0", {"start": v(213.18, 232) * mm, "end": v(213.18, 8) * mm});
            skLineSegment(sketch, "E145.1", {"start": v(213.18, 232) * mm, "end": v(291.68, 232) * mm});
            skLineSegment(sketch, "E145.2", {"start": v(378.18, 232) * mm, "end": v(378.18, 8) * mm});
            skLineSegment(sketch, "E145.3", {"start": v(213.18, 8) * mm, "end": v(291.68, 8) * mm});
            skLineSegment(sketch, "E146.0", {"start": v(510.18, 232) * mm, "end": v(510.18, 8) * mm});
            skLineSegment(sketch, "E146.1", {"start": v(510.18, 232) * mm, "end": v(586.18, 232) * mm});
            skLineSegment(sketch, "E146.2", {"start": v(586.18, 232) * mm, "end": v(586.18, 8) * mm});
            skLineSegment(sketch, "E146.3", {"start": v(510.18, 8) * mm, "end": v(586.18, 8) * mm});
            skLineSegment(sketch, "E147", {"start": v(291.68, 232) * mm, "end": v(291.68, 8) * mm});
            skLineSegment(sketch, "E148", {"start": v(299.68, 232) * mm, "end": v(299.68, 8) * mm});
            skLineSegment(sketch, "E149.trimOffspring", {"start": v(299.68, 232) * mm, "end": v(378.18, 232) * mm});
            skLineSegment(sketch, "E150.trimOffspring", {"start": v(299.68, 8) * mm, "end": v(378.18, 8) * mm});
            skLineSegment(sketch, "E151.0", {"start": v(307.68, 224) * mm, "end": v(307.68, 124) * mm});
            skLineSegment(sketch, "E151.1", {"start": v(307.68, 224) * mm, "end": v(370.18, 224) * mm});
            skLineSegment(sketch, "E151.2", {"start": v(370.18, 224) * mm, "end": v(370.18, 124) * mm});
            skLineSegment(sketch, "E151.3", {"start": v(307.68, 16) * mm, "end": v(370.18, 16) * mm});
            skLineSegment(sketch, "E152", {"start": v(307.68, 124) * mm, "end": v(370.18, 124) * mm});
            skLineSegment(sketch, "E153", {"start": v(307.68, 116) * mm, "end": v(370.18, 116) * mm});
            skLineSegment(sketch, "E154.trimOffspring", {"start": v(370.18, 116) * mm, "end": v(370.18, 16) * mm});
            skLineSegment(sketch, "E155.trimOffspring", {"start": v(307.68, 116) * mm, "end": v(307.68, 16) * mm});
            skSolve(sketch);
        }
        {
            var Q0;
            Q0=makeQuery(id+"F16.imprint","IMPRINT",FACE,{"disambiguationData":[TD([[makeQuery(id+"F16.imprint","IMPRINT",EDGE,{"derivedFrom":sQuery(id+"F16.wireOp",EDGE,"E78.bottom")}),1.0]])]});
            var Q1;
            Q1=makeQuery(id+"F11.imprint","IMPRINT",FACE,{"disambiguationData":[TD([[makeQuery(id+"F11.imprint","IMPRINT",EDGE,{"derivedFrom":sQuery(id+"F11.wireOp",EDGE,"E41")}),-1.0]])]});
            var Q2;
            Q2=makeQuery(id+"F11.imprint","IMPRINT",FACE,{"disambiguationData":[TD([[makeQuery(id+"F11.imprint","IMPRINT",EDGE,{"derivedFrom":sQuery(id+"F11.wireOp",EDGE,"E44")}),-1.0]])]});
            var Q3;
            Q3=makeQuery(id+"F11.imprint","IMPRINT",FACE,{"disambiguationData":[TD([[makeQuery(id+"F11.imprint","IMPRINT",EDGE,{"derivedFrom":sQuery(id+"F11.wireOp",EDGE,"E47")}),-1.0]])]});
            var Q4;
            Q4=makeQuery(id+"F16.imprint","IMPRINT",FACE,{"disambiguationData":[TD([[makeQuery(id+"F16.imprint","IMPRINT",EDGE,{"derivedFrom":sQuery(id+"F16.wireOp",EDGE,"E64")}),-1.0]])]});
            extrude(context, id + "F24", {"entities" : qUnion([Q0, Q1, Q2, Q3, Q4]), "operationType" : NewBodyOperationType.ADD, "depth" : 4 * mm});
        }
        {
            var Q0;
            Q0=makeQuery(id+"F12.imprint","IMPRINT",FACE,{"disambiguationData":[TD([[makeQuery(id+"F12.imprint","IMPRINT",EDGE,{"derivedFrom":sQuery(id+"F12.wireOp",EDGE,"E56.bottom")}),-1.0]])]});
            var Q1;
            Q1=makeQuery(id+"F17.imprint","IMPRINT",FACE,{"disambiguationData":[TD([[makeQuery(id+"F17.imprint","IMPRINT",EDGE,{"derivedFrom":sQuery(id+"F17.wireOp",EDGE,"E86.bottom")}),-1.0]])]});
            var Q2;
            Q2=makeQuery(id+"F17.imprint","IMPRINT",FACE,{"disambiguationData":[TD([[makeQuery(id+"F17.imprint","IMPRINT",EDGE,{"derivedFrom":sQuery(id+"F17.wireOp",EDGE,"E85.bottom")}),-1.0]])]});
            var Q3;
            Q3=makeQuery(id+"F17.imprint","IMPRINT",FACE,{"disambiguationData":[TD([[makeQuery(id+"F17.imprint","IMPRINT",EDGE,{"derivedFrom":sQuery(id+"F17.wireOp",EDGE,"E84.bottom")}),-1.0]])]});
            var Q4;
            Q4=makeQuery(id+"F22.imprint","IMPRINT",FACE,{"disambiguationData":[TD([[makeQuery(id+"F22.imprint","IMPRINT",EDGE,{"derivedFrom":sQuery(id+"F22.wireOp",EDGE,"E139.0")}),1.0]])]});
            extrude(context, id + "F25", {"entities" : qUnion([Q0, Q1, Q2, Q3, Q4]), "operationType" : NewBodyOperationType.ADD, "depth" : 4 * mm});
        }
        {
            var Q0;
            Q0=makeQuery(id+"F19.imprint","IMPRINT",FACE,{"disambiguationData":[TD([[makeQuery(id+"F19.imprint","IMPRINT",EDGE,{"derivedFrom":sQuery(id+"F19.wireOp",EDGE,"E114.bottom")}),1.0]])]});
            var Q1;
            Q1=makeQuery(id+"F21.imprint","IMPRINT",FACE,{"disambiguationData":[TD([[makeQuery(id+"F21.imprint","IMPRINT",EDGE,{"derivedFrom":sQuery(id+"F21.wireOp",EDGE,"E133.bottom")}),-1.0]])]});
            var Q2;
            Q2=makeQuery(id+"F23.imprint","IMPRINT",FACE,{"disambiguationData":[TD([[makeQuery(id+"F23.imprint","IMPRINT",EDGE,{"derivedFrom":sQuery(id+"F23.wireOp",EDGE,"E141.bottom")}),-1.0]])]});
            var Q3;
            Q3=makeQuery(id+"F23.imprint","IMPRINT",FACE,{"disambiguationData":[TD([[makeQuery(id+"F23.imprint","IMPRINT",EDGE,{"derivedFrom":sQuery(id+"F23.wireOp",EDGE,"E143.bottom")}),-1.0]])]});
            var Q4;
            Q4=makeQuery(id+"F23.imprint","IMPRINT",FACE,{"disambiguationData":[TD([[makeQuery(id+"F23.imprint","IMPRINT",EDGE,{"derivedFrom":sQuery(id+"F23.wireOp",EDGE,"E144.bottom")}),-1.0]])]});
            extrude(context, id + "F26", {"entities" : qUnion([Q0, Q1, Q2, Q3, Q4]), "operationType" : NewBodyOperationType.ADD, "depth" : 4 * mm});
        }
        {
            var Q0;
            Q0=makeQuery(id+"F18.imprint","IMPRINT",FACE,{"disambiguationData":[TD([[makeQuery(id+"F18.imprint","IMPRINT",EDGE,{"derivedFrom":sQuery(id+"F18.wireOp",EDGE,"E102.MirrorCS")}),1.0]])]});
            var Q1;
            Q1=makeQuery(id+"F18.imprint","IMPRINT",FACE,{"disambiguationData":[TD([[makeQuery(id+"F18.imprint","IMPRINT",EDGE,{"derivedFrom":sQuery(id+"F18.wireOp",EDGE,"E96.bottom")}),-1.0]])]});
            var Q2;
            Q2=makeQuery(id+"F20.imprint","IMPRINT",FACE,{"disambiguationData":[TD([[makeQuery(id+"F20.imprint","IMPRINT",EDGE,{"derivedFrom":sQuery(id+"F20.wireOp",EDGE,"E120.bottom")}),-1.0]])]});
            var Q3;
            Q3=makeQuery(id+"F20.imprint","IMPRINT",FACE,{"disambiguationData":[TD([[makeQuery(id+"F20.imprint","IMPRINT",EDGE,{"derivedFrom":sQuery(id+"F20.wireOp",EDGE,"E126.bottom")}),-1.0]])]});
            var Q4;
            Q4=makeQuery(id+"F14.imprint","IMPRINT",FACE,{"disambiguationData":[TD([[makeQuery(id+"F14.imprint","IMPRINT",EDGE,{"derivedFrom":sQuery(id+"F14.wireOp",EDGE,"E60.bottom")}),-1.0]])]});
            extrude(context, id + "F27", {"entities" : qUnion([Q0, Q1, Q2, Q3, Q4]), "operationType" : NewBodyOperationType.ADD, "depth" : 4 * mm});
        }
        {
            var Q0;
            Q0=makeQuery(id+"F20.imprint","IMPRINT",FACE,{"disambiguationData":[TD([[makeQuery(id+"F20.imprint","IMPRINT",EDGE,{"derivedFrom":sQuery(id+"F20.wireOp",EDGE,"E127")}),-1.0]])]});
            extrude(context, id + "F28", {"entities" : qUnion([Q0]), "operationType" : NewBodyOperationType.ADD, "depth" : 6 * mm});
        }
    });
